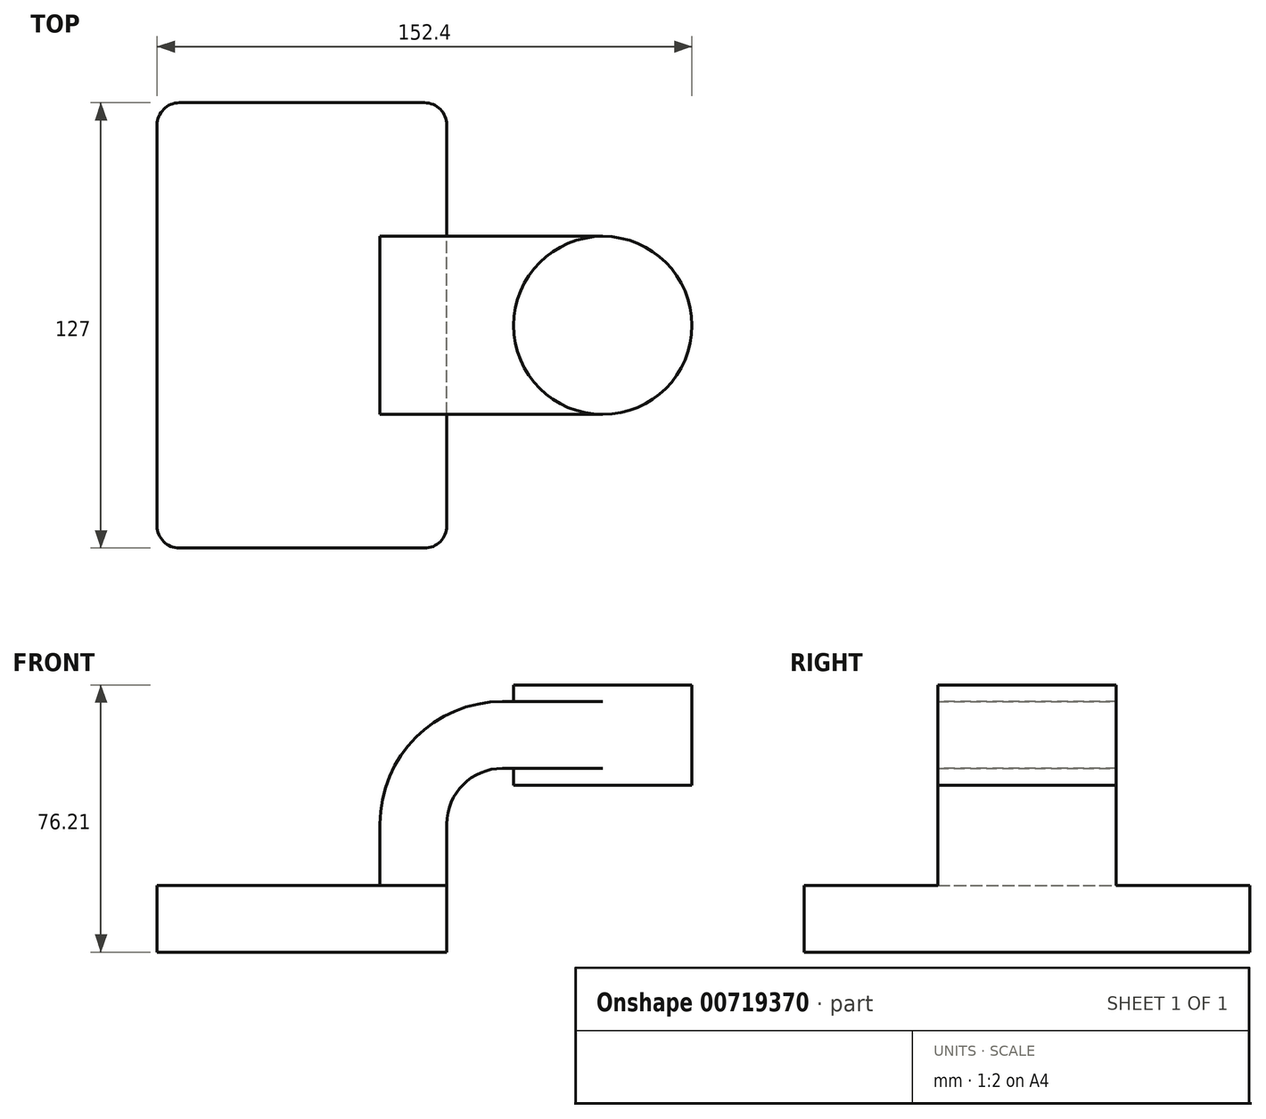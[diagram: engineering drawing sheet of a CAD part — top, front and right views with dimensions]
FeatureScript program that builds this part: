
annotation { "Feature Type Name" : "Feature", "Feature Type Description" : "" }
export const myFeature = defineFeature(function(context is Context, id is Id, definition is map)
    precondition{}
    {
        {
            var Q0;
            Q0=qCreatedBy(makeId("Front.planeOp"),FACE);
            var sketch = newSketch(context, id + "F0", { "sketchPlane" : qUnion([Q0])});
            skLineSegment(sketch, "E0.bottom", {"start": v(41.28, -9.52) * mm, "end": v(-41.28, -9.53) * mm});
            skLineSegment(sketch, "E0.top", {"start": v(41.28, 9.53) * mm, "end": v(-41.28, 9.53) * mm});
            skLineSegment(sketch, "E0.left", {"start": v(41.28, -9.52) * mm, "end": v(41.28, 9.53) * mm});
            skLineSegment(sketch, "E0.right", {"start": v(-41.28, -9.53) * mm, "end": v(-41.28, 9.53) * mm});
            skPoint(sketch, "E0.middle", {"position": v(0, 0) * mm});
            skLineSegment(sketch, "E1.bottom", {"start": v(111.12, 38.1) * mm, "end": v(60.32, 38.1) * mm});
            skLineSegment(sketch, "E1.top", {"start": v(111.12, 66.68) * mm, "end": v(60.32, 66.68) * mm});
            skLineSegment(sketch, "E1.left", {"start": v(111.12, 38.1) * mm, "end": v(111.12, 66.68) * mm});
            skLineSegment(sketch, "E1.right", {"start": v(60.32, 38.1) * mm, "end": v(60.32, 66.68) * mm});
            skPoint(sketch, "E1.middle", {"position": v(85.72, 52.39) * mm});
            skLineSegment(sketch, "E2", {"start": v(41.28, 9.53) * mm, "end": v(41.28, 27) * mm});
            skArc(sketch, "E3", {"start": v(41.27, 27) * mm, "mid": v(45.92, 38.23) * mm, "end": v(57.15, 42.88) * mm});
            skLineSegment(sketch, "E4", {"start": v(57.15, 42.88) * mm, "end": v(101.6, 42.88) * mm});
            skLineSegment(sketch, "E5.0", {"start": v(57.15, 61.93) * mm, "end": v(101.6, 61.93) * mm});
            skArc(sketch, "E5.1", {"start": v(22.23, 27) * mm, "mid": v(32.45, 51.7) * mm, "end": v(57.15, 61.93) * mm});
            skLineSegment(sketch, "E5.2", {"start": v(22.22, 9.53) * mm, "end": v(22.22, 27) * mm});
            skFitSpline(sketch, "E6", {"points": [v(-41.28, 9.52) * mm, v(57.15, 61.93) * mm], "startDerivative": vector(0.79, 119.27) * mm, "endDerivative": vector(139.89, -23.84) * mm});
            skLineSegment(sketch, "E7", {"start": v(85.72, 66.68) * mm, "end": v(85.72, 38.1) * mm});
            skSolve(sketch);
        }
        {
            var Q0;
            Q0=makeQuery(id+"F0.imprint","IMPRINT",FACE,{"disambiguationData":[TD([[makeQuery(id+"F0.imprint","IMPRINT",EDGE,{"derivedFrom":sQuery(id+"F0.wireOp",EDGE,"E0.bottom")}),-1.0]])]});
            extrude(context, id + "F1", {"entities" : qUnion([Q0]), "endBound" : BoundingType.SYMMETRIC, "depth" : 127 * mm, "offsetDistance" : 25.4 * mm});
        }
        {
            var Q0;
            {var subQ1=sQuery(id+"F0.wireOp",EDGE,"E2");Q0=makeQuery(id+"F0.imprint","IMPRINT",FACE,{"disambiguationData":[TD([[makeQuery(id+"F0.imprint","IMPRINT",EDGE,{"derivedFrom":subQ1}),1.0]])]});}
            var Q1;
            {var subQ0=sQuery(id+"F0.wireOp",EDGE,"E4");var subQ1=sQuery(id+"F0.wireOp",EDGE,"E1.right");var subQ2=makeQuery(id+"F0.imprint","INTERSECT",VERTEX,{"derivedFrom":[subQ1,subQ0]});Q1=makeQuery(id+"F0.imprint","IMPRINT",FACE,{"disambiguationData":[TD([[makeQuery(id+"F0.imprint","IMPRINT",EDGE,{"disambiguationData":[TD([[subQ2,-1.0]])],"derivedFrom":subQ1}),-1.0]])]});}
            extrude(context, id + "F2", {"entities" : qUnion([Q0, Q1]), "operationType" : NewBodyOperationType.ADD, "endBound" : BoundingType.SYMMETRIC, "depth" : 50.8 * mm, "offsetDistance" : 25.4 * mm});
        }
        {
            var Q0;
            Q0=makeQuery(id+"F0.imprint","IMPRINT",FACE,{"disambiguationData":[TD([[makeQuery(id+"F0.imprint","IMPRINT",EDGE,{"derivedFrom":sQuery(id+"F0.wireOp",EDGE,"E5.1")}),1.0]])]});
            extrude(context, id + "F3", {"entities" : qUnion([Q0]), "operationType" : NewBodyOperationType.ADD, "endBound" : BoundingType.SYMMETRIC, "depth" : 15.88 * mm, "offsetDistance" : 25.4 * mm});
        }
        {
            var Q0;
            {var subQ0=sQuery(id+"F0.wireOp",EDGE,"E1.left");Q0=makeQuery(id+"F0.imprint","IMPRINT",FACE,{"disambiguationData":[TD([[makeQuery(id+"F0.imprint","IMPRINT",EDGE,{"derivedFrom":subQ0}),1.0]])]});}
            var Q1;
            Q1=sQuery(id+"F0.wireOp",EDGE,"E7");
            revolve(context, id + "F4", {"operationType" : NewBodyOperationType.ADD, "surfaceOperationType" : NewSurfaceOperationType.NEW, "entities" : qUnion([Q0]), "axis" : qUnion([Q1]), "revolveType" : RevolveType.FULL});
        }
        {
            var Q0;
            Q0=makeQuery(id+"F1.opExtrude","CAP_EDGE",EDGE,{"disambiguationData":[OSD([sQuery(id+"F0.wireOp",EDGE,"E0.left")])],"isStart":false});
            var Q1;
            Q1=makeQuery(id+"F1.opExtrude","CAP_EDGE",EDGE,{"disambiguationData":[OSD([sQuery(id+"F0.wireOp",EDGE,"E0.right")])],"isStart":false});
            var Q2;
            Q2=makeQuery(id+"F1.opExtrude","CAP_EDGE",EDGE,{"disambiguationData":[OSD([sQuery(id+"F0.wireOp",EDGE,"E0.left")])],"isStart":true});
            var Q3;
            Q3=makeQuery(id+"F1.opExtrude","CAP_EDGE",EDGE,{"disambiguationData":[OSD([sQuery(id+"F0.wireOp",EDGE,"E0.right")])],"isStart":true});
            fillet(context, id + "F5", {"entities" : qUnion([Q0, Q1, Q2, Q3]), "radius" : 6.35 * mm, "tangentPropagation" : true, "allowEdgeOverflow" : false});
        }
    });
